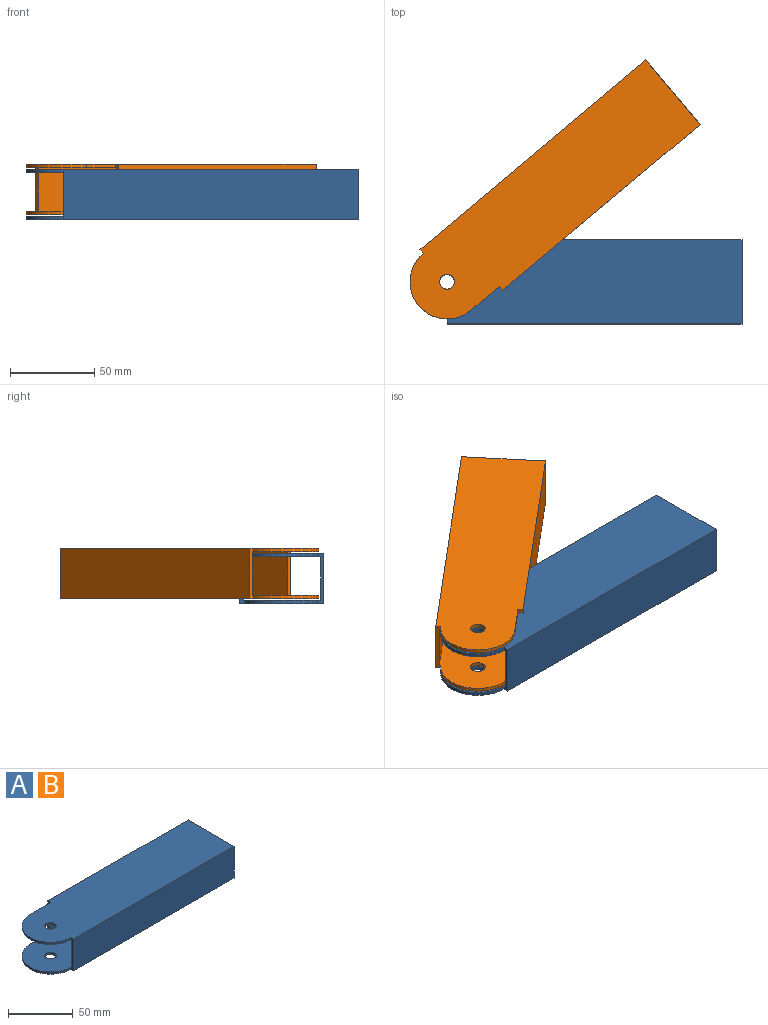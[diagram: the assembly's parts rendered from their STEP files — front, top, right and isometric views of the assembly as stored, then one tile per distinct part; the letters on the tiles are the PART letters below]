
ASSEMBLY  parts=2 mates=1
PART A: 17 faces, bbox 197x50x30 mm
  f0: plane 175x30mm, normal (0,-1,0), area 5250mm2, adj f3,f4,f8,f16
  f1: plane 153x30mm, normal (0,1,0), area 4590mm2, adj f3,f4,f8,f15
  f2: plane 175x26mm, normal (0,1,0), area 4550mm2, adj f5,f7,f8,f16
  f3: plane 197x50mm, normal (0,0,1), area 9384.5mm2, adj f0,f1,f8,f10,f12,f14,f15,f16
  f4: plane 197x50mm, normal (0,0,-1), area 9384.5mm2, adj f0,f1,f8,f9,f11,f13,f15,f16
  f5: plane 197x46mm, normal (0,0,-1), area 8728.5mm2, adj f2,f6,f8,f10,f12,f14,f15,f16
  f6: plane 153x26mm, normal (0,-1,0), area 3978mm2, adj f5,f7,f8,f15
  f7: plane 197x46mm, normal (0,0,1), area 8728.5mm2, adj f2,f6,f8,f9,f11,f13,f15,f16
  f8: plane 50x30mm, normal (1,0,0), area 304mm2, adj f0,f1,f2,f3,f4,f5,f6,f7
  f9: cylinder r=4.36mm len=8.72mm, axis (0,0,1), area 54.8mm2, adj f4,f7
  f10: cylinder r=4.36mm len=8.72mm, axis (0,0,1), area 54.8mm2, adj f3,f5
  f11: cylinder r=22mm len=44mm, axis (0,0,1), area 138.2mm2, adj f4,f7,f13,f16
  f12: cylinder r=22mm len=44mm, axis (0,0,1), area 138.2mm2, adj f3,f5,f14,f16
  f13: plane 22x2mm, normal (0,1,0), area 44mm2, adj f4,f7,f11,f15
  f14: plane 22x2mm, normal (0,1,0), area 44mm2, adj f3,f5,f12,f15
  f15: plane 30x3mm, normal (-1,0,0), area 64mm2, adj f1,f3,f4,f5,f6,f7,f13,f14
  f16: plane 30x3mm, normal (-1,0,0), area 64mm2, adj f0,f2,f3,f4,f5,f7,f11,f12
PART B: same geometry as A
PLACE A t=(-49.57,-13.78,-44)mm fixed
PLACE B rot(axis=(0.94,0.34,0),180deg) t=(-49.57,-13.78,-41)mm
MATE revolute B.f9 <-> A.f9  axis (0,0,-1) through (-49.57,-13.78,-28)mm
